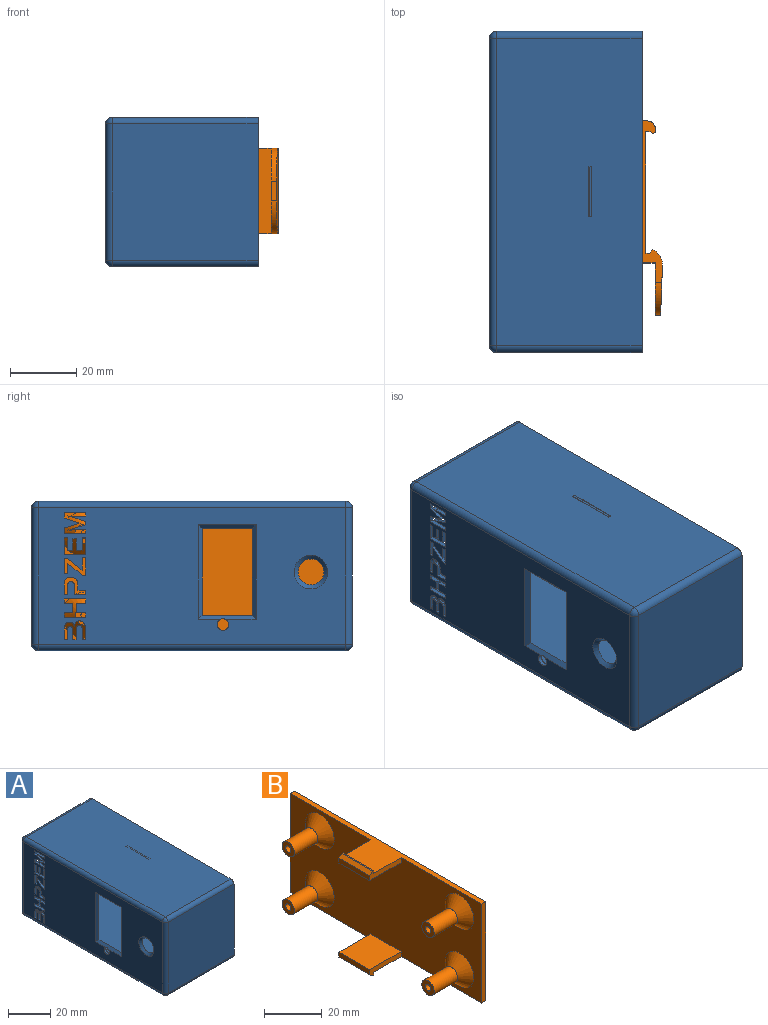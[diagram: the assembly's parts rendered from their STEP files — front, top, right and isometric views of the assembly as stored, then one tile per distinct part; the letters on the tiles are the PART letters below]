
ASSEMBLY  parts=2 mates=1
PART A: 160 faces, bbox 46.2x97.2x45.2 mm
  f0: plane 3.34x1.2mm, normal (0,0,1), area 4mm2, adj f3,f4,f56,f136
  f1: plane 1.2x1.01mm, normal (0,0,1), area 1.2mm2, adj f3,f4,f105,f127
  f2: plane 1.2x1.01mm, normal (0,0,1), area 1.2mm2, adj f3,f4,f119,f126
  f3: plane 94x42mm, normal (1,0,0), area 3347.4mm2, adj f0,f1,f2,f8,f9,f10,f11,f38
  f4: plane 93.2x41.2mm, normal (-1,0,0), area 3122.2mm2, adj f0,f1,f2,f38,f39,f40,f41,f42
  f5: plane 44.2x41.2mm, normal (0,1,0), area 1553mm2, adj f13,f32,f33,f34,f35,f36,f37,f148
  f6: plane 93.2x44.2mm, normal (0,0,-1), area 4119.4mm2, adj f13,f148,f149,f155
  f7: plane 44.2x41.2mm, normal (0,-1,0), area 1821mm2, adj f13,f149,f150,f159
  f8: plane 94x43mm, normal (0,0,-1), area 3800.3mm2, adj f3,f9,f11,f17,f18,f23,f24,f25
  f9: plane 43x42mm, normal (0,1,0), area 1806mm2, adj f3,f8,f10,f17
  f10: plane 94x43mm, normal (0,0,1), area 3805mm2, adj f3,f9,f11,f14,f15,f16,f17,f18
  f11: plane 43x42mm, normal (0,-1,0), area 1538mm2, adj f3,f8,f10,f18,f32,f33,f34,f35
  f12: plane 93.2x44.2mm, normal (0,0,1), area 4119.4mm2, adj f13,f150,f151,f156
  f13: plane 97.2x45.2mm, normal (1,0,0), area 360mm2, adj f5,f6,f7,f12,f19,f20,f21,f22
  f14: plane 15.8x1.5mm, normal (0,-1,0), area 6.7mm2, adj f10,f16,f18,f19,f26,f27,f28
  f15: plane 15.8x1.5mm, normal (0,1,0), area 6.7mm2, adj f10,f16,f17,f19,f26,f27,f28
  f16: plane 15x0.14mm, normal (1,0,0), area 2.2mm2, adj f10,f14,f15,f28
  f17: plane 42.6x39.8mm, normal (1,0,0), area 36.5mm2, adj f8,f9,f10,f15,f19,f20,f21,f24
  f18: plane 42.6x39.8mm, normal (1,0,0), area 36.4mm2, adj f8,f10,f11,f14,f19,f21,f22,f23
  f19: plane 94.6x15.2mm, normal (0,0,1), area 387.2mm2, adj f13,f14,f15,f17,f18,f20,f22,f27
  f20: plane 42.6x2mm, normal (0,1,0), area 85.2mm2, adj f13,f17,f19,f21
  f21: plane 94.6x15.2mm, normal (0,0,-1), area 391.2mm2, adj f13,f17,f18,f20,f22,f23,f24,f29
  f22: plane 42.6x2mm, normal (0,-1,0), area 85.2mm2, adj f13,f18,f19,f21
  f23: plane 15.8x1.5mm, normal (0,-1,0), area 6.7mm2, adj f8,f18,f21,f25,f29,f30,f31
  f24: plane 15.8x1.5mm, normal (0,1,0), area 6.7mm2, adj f8,f17,f21,f25,f29,f30,f31
  f25: plane 15.3x0.14mm, normal (1,0,0), area 2.2mm2, adj f8,f23,f24,f31
  f26: plane 15x0.91mm, normal (0,0,1), area 13.6mm2, adj f14,f15,f27,f28
  f27: plane 15x1.2mm, normal (-1,0,0), area 18mm2, adj f14,f15,f19,f26
  f28: plane 15x1.69mm, normal (0.62,0,0.78), area 32.6mm2, adj f14,f15,f16,f26
  f29: plane 15.3x1.2mm, normal (-1,0,0), area 18.4mm2, adj f21,f23,f24,f30
  f30: plane 15.3x0.91mm, normal (0,0,-1), area 13.9mm2, adj f23,f24,f29,f31
  f31: plane 15.3x1.69mm, normal (0.62,0,-0.78), area 33.2mm2, adj f23,f24,f25,f30
  f32: plane 9.5x1.6mm, normal (1,0,0), area 15.2mm2, adj f5,f11,f33,f37
  f33: plane 8x1.6mm, normal (0,0,1), area 12.8mm2, adj f5,f11,f32,f34
  f34: plane 12.01x1.6mm, normal (1,0,0), area 19.2mm2, adj f5,f11,f33,f35
  f35: plane 16x1.6mm, normal (0,0,-1), area 25.6mm2, adj f5,f11,f34,f36
  f36: plane 21.5x1.6mm, normal (-1,0,0), area 34.4mm2, adj f5,f11,f35,f37
  f37: plane 8x1.6mm, normal (0,0,1), area 12.8mm2, adj f5,f11,f32,f36
  f38: cylinder r=1.75mm len=3.5mm, axis (-1,0,0), area 13.1mm2, adj f3,f4,f143
  f39: plane 2.79x1.2mm, normal (0,0,1), area 3.4mm2, adj f3,f4,f40,f50
  f40: plane 1.36x1.2mm, normal (0,1,0), area 1.6mm2, adj f3,f4,f39,f41
  f41: plane 6.51x1.2mm, normal (0,0,-1), area 7.8mm2, adj f3,f4,f40,f42
  f42: plane 1.36x1.2mm, normal (0,-1,0), area 1.6mm2, adj f3,f4,f41,f43
  f43: plane 2.59x1.2mm, normal (0,0,1), area 3.1mm2, adj f3,f4,f42,f44
  f44: plane 2.84x1.2mm, normal (0,-1,0), area 3.4mm2, adj f3,f4,f43,f45
  f45: plane 2.59x1.2mm, normal (0,0,-1), area 3.1mm2, adj f3,f4,f44,f46
  f46: plane 1.36x1.2mm, normal (0,-1,0), area 1.6mm2, adj f3,f4,f45,f47
  f47: plane 6.51x1.2mm, normal (0,0,1), area 7.8mm2, adj f3,f4,f46,f48
  f48: plane 1.36x1.2mm, normal (0,1,0), area 1.6mm2, adj f3,f4,f47,f49
  f49: plane 2.79x1.2mm, normal (0,0,-1), area 3.4mm2, adj f3,f4,f48,f50
  f50: plane 2.84x1.2mm, normal (0,1,0), area 3.4mm2, adj f3,f4,f39,f49
  f51: extruded ~1.2x1.12mm, area 1.4mm2, adj f3,f4,f52,f60
  f52: extruded ~1.52x1.2mm, area 2mm2, adj f3,f4,f51,f53
  f53: extruded ~1.8x1.2mm, area 2.3mm2, adj f3,f4,f52,f54
  f54: plane 2.93x1.2mm, normal (0,-1,0), area 3.5mm2, adj f3,f4,f53,f55
  f55: plane 1.2x1.06mm, normal (0,0,1), area 1.3mm2, adj f3,f4,f54,f135
  f56: plane 1.36x1.2mm, normal (0,1,0), area 1.6mm2, adj f0,f3,f4,f57
  f57: plane 2.29x1.2mm, normal (0,0,-1), area 2.8mm2, adj f3,f4,f56,f58
  f58: plane 1.62x1.2mm, normal (0,1,0), area 1.9mm2, adj f3,f4,f57,f59
  f59: extruded ~1.27x1.2mm, area 1.6mm2, adj f3,f4,f58,f60
  f60: extruded ~1.2x0.82mm, area 1.4mm2, adj f3,f4,f51,f59
  f61: plane 3.95x1.2mm, normal (0,0,1), area 4.7mm2, adj f3,f4,f62,f81
  f62: plane 1.21x1.2mm, normal (0,1,0), area 1.5mm2, adj f3,f4,f61,f63
  f63: plane 6.51x1.2mm, normal (0,0,-1), area 7.8mm2, adj f3,f4,f62,f64
  f64: plane 1.82x1.2mm, normal (0,-1,0), area 2.2mm2, adj f3,f4,f63,f65
  f65: plane 3.82x1.2mm, normal (0,-0.3,0.95), area 4.8mm2, adj f3,f4,f64,f66
  f66: plane 1.2x1.04mm, normal (0,-0.27,0.96), area 1.3mm2, adj f3,f4,f65,f67
  f67: plane 1.2x0.87mm, normal (0,-0.25,-0.97), area 1.1mm2, adj f3,f4,f66,f68
  f68: plane 1.2x0.35mm, normal (0,-0.28,-0.96), area 0.4mm2, adj f3,f4,f67,f69
  f69: plane 3.64x1.2mm, normal (0,-0.3,-0.95), area 4.6mm2, adj f3,f4,f68,f70
  f70: plane 1.83x1.2mm, normal (0,-1,0), area 2.2mm2, adj f3,f4,f69,f71
  f71: plane 6.51x1.2mm, normal (0,0,1), area 7.8mm2, adj f3,f4,f70,f72
  f72: plane 1.21x1.2mm, normal (0,1,0), area 1.5mm2, adj f3,f4,f71,f73
  f73: plane 3.95x1.2mm, normal (0,0,-1), area 4.7mm2, adj f3,f4,f72,f74
  f74: extruded ~1.42x1.2mm, area 1.7mm2, adj f3,f4,f73,f75
  f75: plane 1.73x1.2mm, normal (0,0.27,0.96), area 2.2mm2, adj f3,f4,f74,f76
  f76: plane 3.63x1.2mm, normal (0,0.31,0.95), area 4.6mm2, adj f3,f4,f75,f77
  f77: plane 1.2x0.97mm, normal (0,1,0), area 1.2mm2, adj f3,f4,f76,f78
  f78: plane 3.63x1.2mm, normal (0,0.31,-0.95), area 4.6mm2, adj f3,f4,f77,f79
  f79: extruded ~1.73x1.2mm, area 2.2mm2, adj f3,f4,f78,f80
  f80: extruded ~1.2x1.15mm, area 1.4mm2, adj f3,f4,f79,f81
  f81: extruded ~1.2x0.27mm, area 0.3mm2, adj f3,f4,f61,f80
  f82: plane 6.51x1.2mm, normal (0,0,1), area 7.8mm2, adj f3,f4,f83,f93
  f83: plane 5.31x1.2mm, normal (0,1,0), area 6.4mm2, adj f3,f4,f82,f84
  f84: plane 1.2x1.06mm, normal (0,0,-1), area 1.3mm2, adj f3,f4,f83,f85
  f85: plane 3.95x1.2mm, normal (0,-1,0), area 4.7mm2, adj f3,f4,f84,f86
  f86: plane 1.71x1.2mm, normal (0,0,-1), area 2.1mm2, adj f3,f4,f85,f87
  f87: plane 3.48x1.2mm, normal (0,1,0), area 4.2mm2, adj f3,f4,f86,f88
  f88: plane 1.2x1.05mm, normal (0,0,-1), area 1.3mm2, adj f3,f4,f87,f89
  f89: plane 3.48x1.2mm, normal (0,-1,0), area 4.2mm2, adj f3,f4,f88,f90
  f90: plane 1.64x1.2mm, normal (0,0,-1), area 2mm2, adj f3,f4,f89,f91
  f91: plane 3.76x1.2mm, normal (0,1,0), area 4.5mm2, adj f3,f4,f90,f92
  f92: plane 1.2x1.05mm, normal (0,0,-1), area 1.3mm2, adj f3,f4,f91,f93
  f93: plane 5.12x1.2mm, normal (0,-1,0), area 6.1mm2, adj f3,f4,f82,f92
  f94: plane 5.23x1.2mm, normal (0,1,0), area 6.3mm2, adj f3,f4,f95,f103
  f95: plane 1.2x1.07mm, normal (0,0,-1), area 1.3mm2, adj f3,f4,f94,f96
  f96: plane 3.71x1.2mm, normal (0,-1,0), area 4.5mm2, adj f3,f4,f95,f97
  f97: plane 4.5x3.52mm, normal (0,0.62,-0.79), area 6.9mm2, adj f3,f4,f96,f98
  f98: plane 1.2x0.95mm, normal (0,0,-1), area 1.1mm2, adj f3,f4,f97,f99
  f99: plane 4.69x1.2mm, normal (0,-1,0), area 5.6mm2, adj f3,f4,f98,f100
  f100: plane 1.2x1.07mm, normal (0,0,1), area 1.3mm2, adj f3,f4,f99,f101
  f101: plane 3.17x1.2mm, normal (0,1,0), area 3.8mm2, adj f3,f4,f100,f102
  f102: plane 4.48x3.52mm, normal (0,-0.62,0.79), area 6.8mm2, adj f3,f4,f101,f103
  f103: plane 1.2x0.97mm, normal (0,0,1), area 1.2mm2, adj f3,f4,f94,f102
  f104: extruded ~1.85x1.2mm, area 2.3mm2, adj f3,f4,f105,f114
  f105: plane 3.26x1.2mm, normal (0,1,0), area 3.9mm2, adj f1,f3,f4,f104
  f106: plane 1.2x1.01mm, normal (0,0,1), area 1.2mm2, adj f3,f4,f107,f120
  f107: plane 2.98x1.2mm, normal (0,-1,0), area 3.6mm2, adj f3,f4,f106,f108
  f108: extruded ~1.81x1.2mm, area 2.3mm2, adj f3,f4,f107,f109
  f109: extruded ~1.22x1.2mm, area 1.7mm2, adj f3,f4,f108,f110
  f110: extruded ~1.2x0.94mm, area 1.2mm2, adj f3,f4,f109,f111
  f111: extruded ~1.2x0.94mm, area 1.3mm2, adj f3,f4,f110,f112
  f112: extruded ~1.2x1.2mm, area 1.6mm2, adj f3,f4,f111,f113
  f113: extruded ~1.2x1.07mm, area 1.4mm2, adj f3,f4,f112,f114
  f114: extruded ~1.37x1.2mm, area 1.9mm2, adj f3,f4,f104,f113
  f115: plane 1.61x0.8mm, normal (0,0,-1), area 1.3mm2, adj f3,f119,f120,f124
  f116: extruded ~1.2x0.62mm, area 0.9mm2, adj f4,f117,f121,f122
  f117: extruded ~1.2x0.6mm, area 0.8mm2, adj f4,f116,f118,f122
  f118: extruded ~1.2x0.84mm, area 1.1mm2, adj f4,f117,f119,f122
  f119: plane 2.93x2mm, normal (0,-1,0), area 4.6mm2, adj f2,f4,f115,f118,f122,f123,f124
  f120: plane 2.92x2mm, normal (0,1,0), area 4.6mm2, adj f4,f106,f115,f121,f122,f123,f124
  f121: extruded ~1.2x0.83mm, area 1mm2, adj f4,f116,f120,f122
  f122: plane 2.66x1.61mm, normal (1,0,0), area 4mm2, adj f116,f117,f118,f119,f120,f121,f123
  f123: plane 1.61x0.8mm, normal (0,0,1), area 1.3mm2, adj f119,f120,f122,f124
  f124: plane 1.61x1.36mm, normal (1,0,0), area 2.2mm2, adj f115,f119,f120,f123
  f125: plane 1.87x0.8mm, normal (0,0,-1), area 1.5mm2, adj f3,f126,f127,f133
  f126: plane 3.09x2mm, normal (0,1,0), area 4.8mm2, adj f2,f4,f125,f130,f131,f132,f133
  f127: plane 3.14x2mm, normal (0,-1,0), area 4.9mm2, adj f1,f4,f125,f128,f131,f132,f133
  f128: extruded ~1.2x0.96mm, area 1.2mm2, adj f4,f127,f129,f131
  f129: extruded ~1.2x0.71mm, area 1mm2, adj f4,f128,f130,f131
  f130: extruded ~1.31x1.2mm, area 2.2mm2, adj f4,f126,f129,f131
  f131: plane 3.04x1.87mm, normal (1,0,0), area 5.3mm2, adj f126,f127,f128,f129,f130,f132
  f132: plane 1.87x0.8mm, normal (0,0,1), area 1.5mm2, adj f126,f127,f131,f133
  f133: plane 1.87x1.36mm, normal (1,0,0), area 2.5mm2, adj f125,f126,f127,f132
  f134: plane 2.11x0.8mm, normal (0,0,-1), area 1.7mm2, adj f3,f135,f136,f142
  f135: plane 2.77x2mm, normal (0,1,0), area 4.4mm2, adj f4,f55,f134,f139,f140,f141,f142
  f136: plane 2.81x2mm, normal (0,-1,0), area 4.5mm2, adj f0,f4,f134,f137,f140,f141,f142
  f137: extruded ~1.2x0.87mm, area 1.1mm2, adj f4,f136,f138,f140
  f138: extruded ~1.2x0.81mm, area 1.1mm2, adj f4,f137,f139,f140
  f139: extruded ~1.21x1.2mm, area 2.2mm2, adj f4,f135,f138,f140
  f140: plane 2.62x2.11mm, normal (1,0,0), area 5.1mm2, adj f135,f136,f137,f138,f139,f141
  f141: plane 2.11x0.8mm, normal (0,0,1), area 1.7mm2, adj f135,f136,f140,f142
  f142: plane 2.11x1.36mm, normal (1,0,0), area 2.9mm2, adj f134,f135,f136,f141
  f143: plane 17.6x1.2mm, normal (-0.71,0,0.71), area 27.6mm2, adj f3,f4,f38,f144,f145
  f144: plane 28.65x1.2mm, normal (-0.71,-0.71,0), area 46.6mm2, adj f3,f4,f143,f146
  f145: plane 28.65x1.2mm, normal (-0.71,0.71,0), area 46.6mm2, adj f3,f4,f143,f146
  f146: plane 17.6x1.2mm, normal (-0.71,0,-0.71), area 27.8mm2, adj f3,f4,f144,f145
  f147: cone r=3.1mm half-angle=45deg, axis (-1,0,0), area 48mm2, adj f3,f4
  f148: cylinder r=2mm len=44.2mm, axis (1,0,0), area 138.9mm2, adj f5,f6,f13,f153
  f149: cylinder r=2mm len=44.2mm, axis (-1,0,0), area 138.9mm2, adj f6,f7,f13,f157
  f150: cylinder r=2mm len=44.2mm, axis (1,0,0), area 138.9mm2, adj f7,f12,f13,f158
  f151: cylinder r=2mm len=44.2mm, axis (-1,0,0), area 138.9mm2, adj f5,f12,f13,f154
  f152: cylinder r=2mm len=41.2mm, axis (0,0,1), area 129.4mm2, adj f4,f5,f153,f154
  f153: sphere r=2mm, area 6.3mm2, adj f148,f152,f155
  f154: sphere r=2mm, area 6.3mm2, adj f151,f152,f156
  f155: cylinder r=2mm len=93.2mm, axis (0,1,0), area 292.8mm2, adj f4,f6,f153,f157
  f156: cylinder r=2mm len=93.2mm, axis (0,-1,0), area 292.8mm2, adj f4,f12,f154,f158
  f157: sphere r=2mm, area 6.3mm2, adj f149,f155,f159
  f158: sphere r=2mm, area 6.3mm2, adj f150,f156,f159
  f159: cylinder r=2mm len=41.2mm, axis (0,0,-1), area 129.4mm2, adj f4,f7,f157,f158
PART B: 60 faces, bbox 23.6x94x44.4 mm
  f0: plane 94x42mm, normal (-1,0,0), area 3269.3mm2, adj f19,f20,f21,f22,f39,f40,f41,f43
  f1: plane 26x0.74mm, normal (1,0,0), area 19.2mm2, adj f2,f14,f15,f17
  f2: cylinder r=2.4mm len=26mm, axis (0,0,-1), area 98mm2, adj f1,f3,f14,f15
  f3: plane 26x1.54mm, normal (0,1,0), area 39.9mm2, adj f2,f14,f15,f18
  f4: plane 26x3.94mm, normal (0,-1,0), area 102.3mm2, adj f5,f14,f15,f18
  f5: plane 26x15.84mm, normal (-1,0,0), area 368.9mm2, adj f4,f6,f14,f15,f57,f58
  f6: plane 6x1.6mm, normal (0,-1,0), area 9.6mm2, adj f5,f7,f57,f58
  f7: plane 26x15.08mm, normal (1,-0.04,0), area 349.5mm2, adj f6,f14,f15,f57,f58,f59
  f8: plane 26x1.11mm, normal (-0.75,0.66,0), area 38.5mm2, adj f9,f14,f15,f59
  f9: plane 26x1.17mm, normal (0,1,0), area 30.3mm2, adj f8,f10,f14,f15
  f10: plane 36.83x26mm, normal (1,0,0), area 957.7mm2, adj f9,f11,f14,f15
  f11: plane 26x1.3mm, normal (0,-1,0), area 33.8mm2, adj f10,f12,f14,f15
  f12: plane 26x0.62mm, normal (-0.63,-0.78,0), area 20.6mm2, adj f11,f14,f15,f16
  f13: plane 26x0.35mm, normal (0.72,-0.69,0), area 12.5mm2, adj f14,f15,f16,f17
  f14: plane 48.84x6.1mm, normal (0,0,1), area 80.2mm2, adj f1,f2,f3,f4,f5,f7,f8,f9
  f15: plane 48.84x6.1mm, normal (0,0,-1), area 80.2mm2, adj f1,f2,f3,f4,f5,f7,f8,f9
  f16: cylinder r=0.4mm len=26mm, axis (0,0,-1), area 15.4mm2, adj f12,f13,f14,f15
  f17: cylinder r=0.4mm len=26mm, axis (0,0,1), area 8mm2, adj f1,f13,f14,f15
  f18: plane 94x42mm, normal (1,0,0), area 2830mm2, adj f3,f4,f14,f15,f19,f20,f21,f22
  f19: plane 94x15.5mm, normal (0,0,-1), area 390.5mm2, adj f0,f18,f20,f22,f43,f44,f52
  f20: plane 42x2mm, normal (0,-1,0), area 84mm2, adj f0,f18,f19,f21
  f21: plane 94x15.5mm, normal (0,0,1), area 390.5mm2, adj f0,f18,f20,f22,f39,f41,f54
  f22: plane 42x2mm, normal (0,1,0), area 84mm2, adj f0,f18,f19,f21
  f23: cylinder r=1.3mm len=15.5mm, axis (1,0,0), area 126.6mm2, adj f25,f26
  f24: cylinder r=3mm len=11.5mm, axis (1,0,0), area 216.8mm2, adj f25,f47
  f25: plane 6x6mm, normal (-1,0,0), area 23mm2, adj f23,f24
  f26: plane 2.6x2.6mm, normal (-1,0,0), area 5.3mm2, adj f23
  f27: cylinder r=1.3mm len=15.5mm, axis (1,0,0), area 126.6mm2, adj f29,f30
  f28: cylinder r=3mm len=11.5mm, axis (1,0,0), area 216.8mm2, adj f29,f48
  f29: plane 6x6mm, normal (-1,0,0), area 23mm2, adj f27,f28
  f30: plane 2.6x2.6mm, normal (-1,0,0), area 5.3mm2, adj f27
  f31: cylinder r=1.3mm len=15.5mm, axis (1,0,0), area 126.6mm2, adj f33,f34
  f32: cylinder r=3mm len=11.5mm, axis (1,0,0), area 216.8mm2, adj f33,f50
  f33: plane 6x6mm, normal (-1,0,0), area 23mm2, adj f31,f32
  f34: plane 2.6x2.6mm, normal (-1,0,0), area 5.3mm2, adj f31
  f35: cylinder r=1.3mm len=15.5mm, axis (1,0,0), area 126.6mm2, adj f37,f38
  f36: cylinder r=3mm len=11.5mm, axis (1,0,0), area 216.8mm2, adj f37,f49
  f37: plane 6x6mm, normal (-1,0,0), area 23mm2, adj f35,f36
  f38: plane 2.6x2.6mm, normal (-1,0,0), area 5.3mm2, adj f35
  f39: plane 15.5x3.3mm, normal (0,1,0), area 34mm2, adj f0,f21,f40,f42,f54,f55,f56
  f40: plane 15.5x15mm, normal (0,0,-1), area 232.5mm2, adj f0,f39,f41,f42
  f41: plane 15.5x3.3mm, normal (0,-1,0), area 34mm2, adj f0,f21,f40,f42,f54,f55,f56
  f42: plane 15x2.1mm, normal (-1,0,0), area 31.5mm2, adj f39,f40,f41,f56
  f43: plane 15.5x3.3mm, normal (0,1,0), area 34mm2, adj f0,f19,f45,f46,f51,f52,f53
  f44: plane 15.5x3.3mm, normal (0,-1,0), area 34mm2, adj f0,f19,f45,f46,f51,f52,f53
  f45: plane 15.5x15mm, normal (0,0,1), area 232.5mm2, adj f0,f43,f44,f46
  f46: plane 15x2.1mm, normal (-1,0,0), area 31.5mm2, adj f43,f44,f45,f53
  f47: cone r=3mm half-angle=45deg, axis (1,0,0), area 177.7mm2, adj f0,f24
  f48: cone r=3mm half-angle=45deg, axis (1,0,0), area 177.7mm2, adj f0,f28
  f49: cone r=3mm half-angle=45deg, axis (1,0,0), area 177.7mm2, adj f0,f36
  f50: cone r=3mm half-angle=45deg, axis (1,0,0), area 177.7mm2, adj f0,f32
  f51: plane 15x0.5mm, normal (0,0,-1), area 7.5mm2, adj f43,f44,f52,f53
  f52: plane 15x1.2mm, normal (1,0,0), area 18mm2, adj f19,f43,f44,f51
  f53: plane 15x1.5mm, normal (-0.62,0,-0.78), area 28.8mm2, adj f43,f44,f46,f51
  f54: plane 15x1.2mm, normal (1,0,0), area 18mm2, adj f21,f39,f41,f55
  f55: plane 15x0.5mm, normal (0,0,1), area 7.5mm2, adj f39,f41,f54,f56
  f56: plane 15x1.5mm, normal (-0.62,0,0.78), area 28.8mm2, adj f39,f41,f42,f55
  f57: cylinder r=10mm len=10mm, axis (1,0,0), area 27.3mm2, adj f5,f6,f7,f15
  f58: cylinder r=10mm len=10mm, axis (-1,0,0), area 27.3mm2, adj f5,f6,f7,f14
  f59: cylinder r=5mm len=26mm, axis (0,0,1), area 153.1mm2, adj f7,f8,f14,f15
PLACE A rot(axis=(0,0,1),0deg) t=(52.72,5.22,-11.96)mm
PLACE B rot(axis=(0,0,1),0deg) t=(52.79,5.22,-11.66)mm fixed
MATE slider B.f18 <-> A.f13  axis (1,0,0) through (56.1,5.22,-11.66)mm
